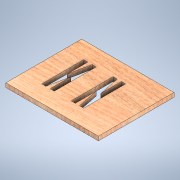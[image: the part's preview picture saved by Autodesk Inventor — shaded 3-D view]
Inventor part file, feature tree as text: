
AUTODESK INVENTOR PART (.ipt)
format: ipt  version: 2022 (Build 260153000, 153)  size: 175,104 bytes
history: native  units: mm
features: sketch x4, extrude x2, other x1
ambient origin geometry x8: Origin, YZ Plane, XZ Plane, XY Plane, X Axis, Y Axis, Z Axis, Center Point
bodies: Body1 (feature_tree)
feature tree (7):
  other  "Sólido1"
  sketch  "Boceto1"  dims[d0=220.0mm d1=180.0mm]
  extrude  "Extrusión1"  Depth=180.0mm
  sketch  "Boceto3"  dims[d4=50.0mm]
  extrude  "Extrusión2"  TaperAngle=0.0deg  [1 undecoded]
  sketch  "Boceto2"  dims[d2=10.0mm d3=0.0mm]
  sketch  "Boceto4"  dims[d5=0.0mm d6=10.0mm d7=100.0mm d8=10.0mm d10=100.0mm d11=100.0mm d12=10.0mm d13=100.0mm d14=20.0mm d15=20.0mm d16=10.0mm d17=0.0mm]
note: 1 required parameter value undecoded (feature->parameter linkage not recoverable at this tier; creation-order binding heuristic only, values carry confidence <= 0.55)
